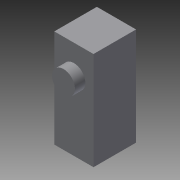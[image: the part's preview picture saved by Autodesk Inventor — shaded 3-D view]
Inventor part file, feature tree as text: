
AUTODESK INVENTOR PART (.ipt)
format: ipt  version: 2013 (Build 170138000, 138)  size: 83,968 bytes
history: native  units: in
note: dims shown in document units (in); Inventor stores cm internally (conversion verified against a paired STEP export)
features: extrude x2, sketch x2
ambient origin geometry x8: Origin, YZ Plane, XZ Plane, XY Plane, X Axis, Y Axis, Z Axis, Center Point
bodies: Solid1 (feature_tree)
feature tree (4):
  extrude  "Extrusion1"  Depth=1.1811in
  extrude  "Extrusion2"  TaperAngle=0.0deg  [1 undecoded]
  sketch  "Sketch1"  dims[d0=0.4724in d1=1.1811in]
  sketch  "Sketch2"  dims[d2=0.513in d3=0.0in d4=0.2362in d5=0.35in d6=0.125in d7=0.0in d8=0.276in]
note: 1 required parameter value undecoded (feature->parameter linkage not recoverable at this tier; creation-order binding heuristic only, values carry confidence <= 0.55)
